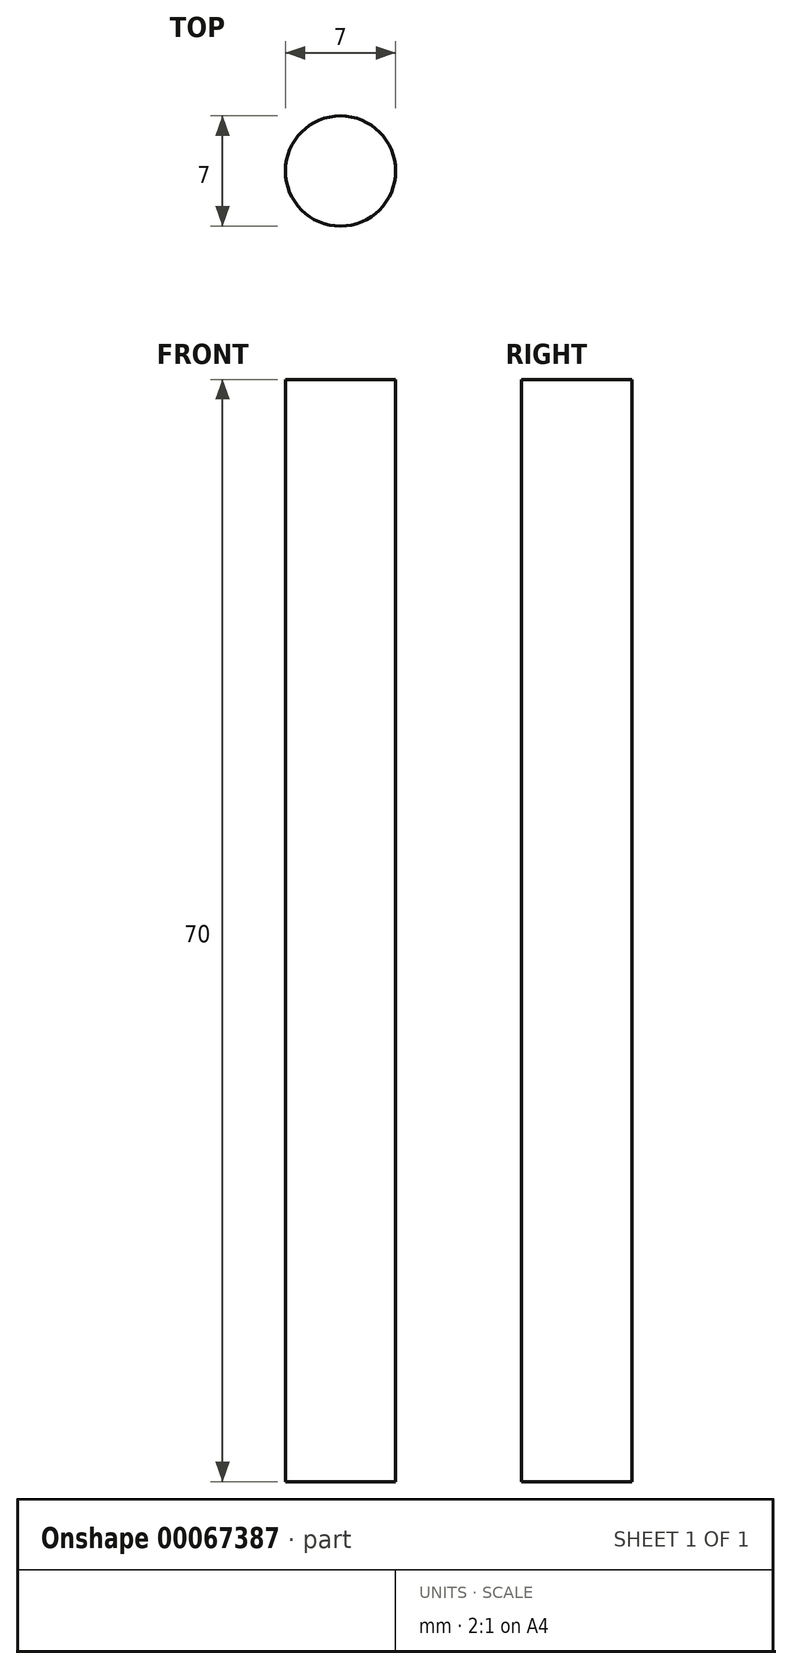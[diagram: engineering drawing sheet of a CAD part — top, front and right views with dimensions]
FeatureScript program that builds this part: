
annotation { "Feature Type Name" : "Feature", "Feature Type Description" : "" }
export const myFeature = defineFeature(function(context is Context, id is Id, definition is map)
    precondition{}
    {
        {
            var Q0;
            Q0=qCreatedBy(makeId("Top.planeOp"),FACE);
            var sketch = newSketch(context, id + "F0", { "sketchPlane" : qUnion([Q0])});
            skCircle(sketch, "E0", {"center": v(0, 0) * mm, "radius": 3.5 * mm});
            skSolve(sketch);
        }
        {
            var Q0;
            Q0 = qSketchRegion(id + "F0", true);
            extrude(context, id + "F1", {"entities" : qUnion([Q0]), "depth" : 70 * mm});
        }
    });
